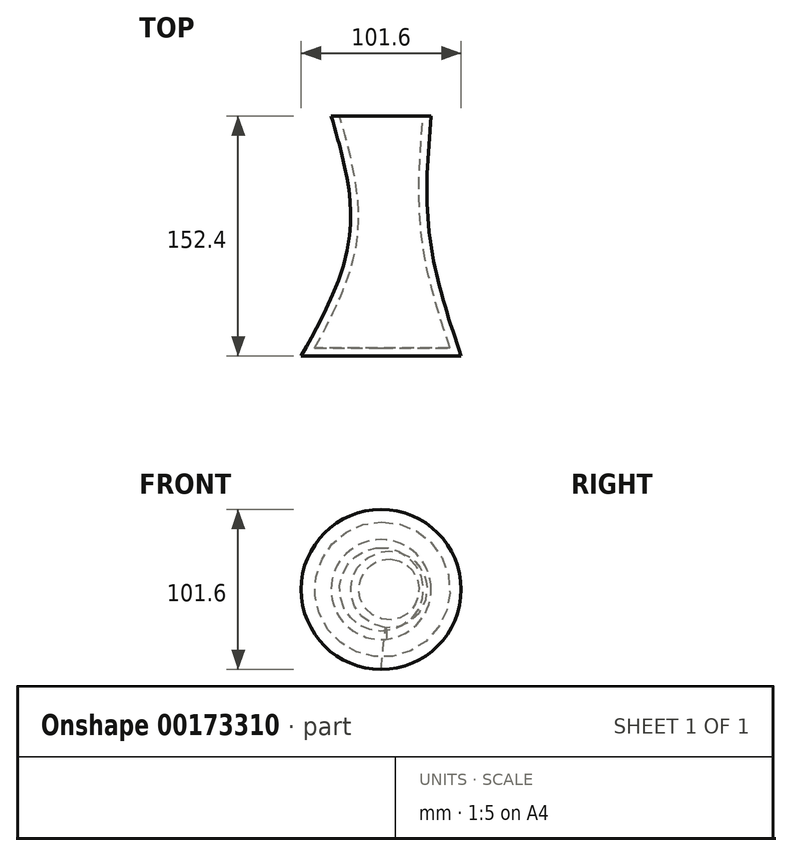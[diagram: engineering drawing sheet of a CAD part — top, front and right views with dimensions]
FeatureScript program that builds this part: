
annotation { "Feature Type Name" : "Feature", "Feature Type Description" : "" }
export const myFeature = defineFeature(function(context is Context, id is Id, definition is map)
    precondition{}
    {
        {
            var Q0;
            Q0=qCreatedBy(makeId("Front.planeOp"),FACE);
            cPlane(context, id + "F0", {"entities" : qUnion([Q0]), "cplaneType" : CPlaneType.OFFSET, "offset" : 0 * mm, "width" : 152.4 * mm, "height" : 152.4 * mm});
        }
        {
            var Q0;
            Q0=qCreatedBy(id+"F0.planeOp",FACE);
            cPlane(context, id + "F1", {"entities" : qUnion([Q0]), "cplaneType" : CPlaneType.OFFSET, "offset" : 76.2 * mm, "width" : 152.4 * mm, "height" : 152.4 * mm});
        }
        {
            var Q0;
            Q0=qCreatedBy(id+"F1.planeOp",FACE);
            cPlane(context, id + "F2", {"entities" : qUnion([Q0]), "cplaneType" : CPlaneType.OFFSET, "offset" : 76.2 * mm, "width" : 152.4 * mm, "height" : 152.4 * mm});
        }
        {
            var Q0;
            Q0=qCreatedBy(id+"F0.planeOp",FACE);
            var sketch = newSketch(context, id + "F3", { "sketchPlane" : qUnion([Q0])});
            skCircle(sketch, "E0", {"center": v(0, 0) * mm, "radius": 31.75 * mm});
            skSolve(sketch);
        }
        {
            var Q0;
            Q0=qCreatedBy(id+"F1.planeOp",FACE);
            var sketch = newSketch(context, id + "F4", { "sketchPlane" : qUnion([Q0])});
            skPoint(sketch, "E1.middle", {"position": v(5.38, 0) * mm});
            skCircle(sketch, "E2", {"center": v(5.38, 0) * mm, "radius": 25.4 * mm});
            skSolve(sketch);
        }
        {
            var Q0;
            Q0=qCreatedBy(id+"F2.planeOp",FACE);
            var sketch = newSketch(context, id + "F5", { "sketchPlane" : qUnion([Q0])});
            skPoint(sketch, "E3.middle", {"position": v(0, 0) * mm});
            skCircle(sketch, "E4", {"center": v(0, 0) * mm, "radius": 50.8 * mm});
            skSolve(sketch);
        }
        {
            var Q0;
            Q0=makeQuery(id+"F5.imprint","IMPRINT",FACE,{"disambiguationData":[TD([[makeQuery(id+"F5.imprint","IMPRINT",EDGE,{"derivedFrom":sQuery(id+"F5.wireOp",EDGE,"E4")}),1.0]])]});
            var Q1;
            Q1=makeQuery(id+"F4.imprint","IMPRINT",FACE,{"disambiguationData":[TD([[makeQuery(id+"F4.imprint","IMPRINT",EDGE,{"derivedFrom":sQuery(id+"F4.wireOp",EDGE,"E2")}),1.0]])]});
            var Q2;
            Q2=makeQuery(id+"F3.imprint","IMPRINT",FACE,{"disambiguationData":[TD([[makeQuery(id+"F3.imprint","IMPRINT",EDGE,{"derivedFrom":sQuery(id+"F3.wireOp",EDGE,"E0")}),1.0]])]});
            loft(context, id + "F6", {"sheetProfilesArray" : [{ "sheetProfileEntities" : qUnion([Q0]) }, { "sheetProfileEntities" : qUnion([Q1]) }, { "sheetProfileEntities" : qUnion([Q2]) }]});
        }
        {
            var Q0;
            Q0=makeQuery(id+"F6.opLoft","CAP_FACE",FACE,{"disambiguationData":[OSD([makeQuery(id+"F3.imprint","IMPRINT",FACE,{"disambiguationData":[TD([[makeQuery(id+"F3.imprint","IMPRINT",EDGE,{"derivedFrom":sQuery(id+"F3.wireOp",EDGE,"E0")}),1.0]])]})])],"isStart":true});
            shell(context, id + "F7", {"entities" : qUnion([Q0]), "thickness" : 5.08 * mm});
        }
    });
